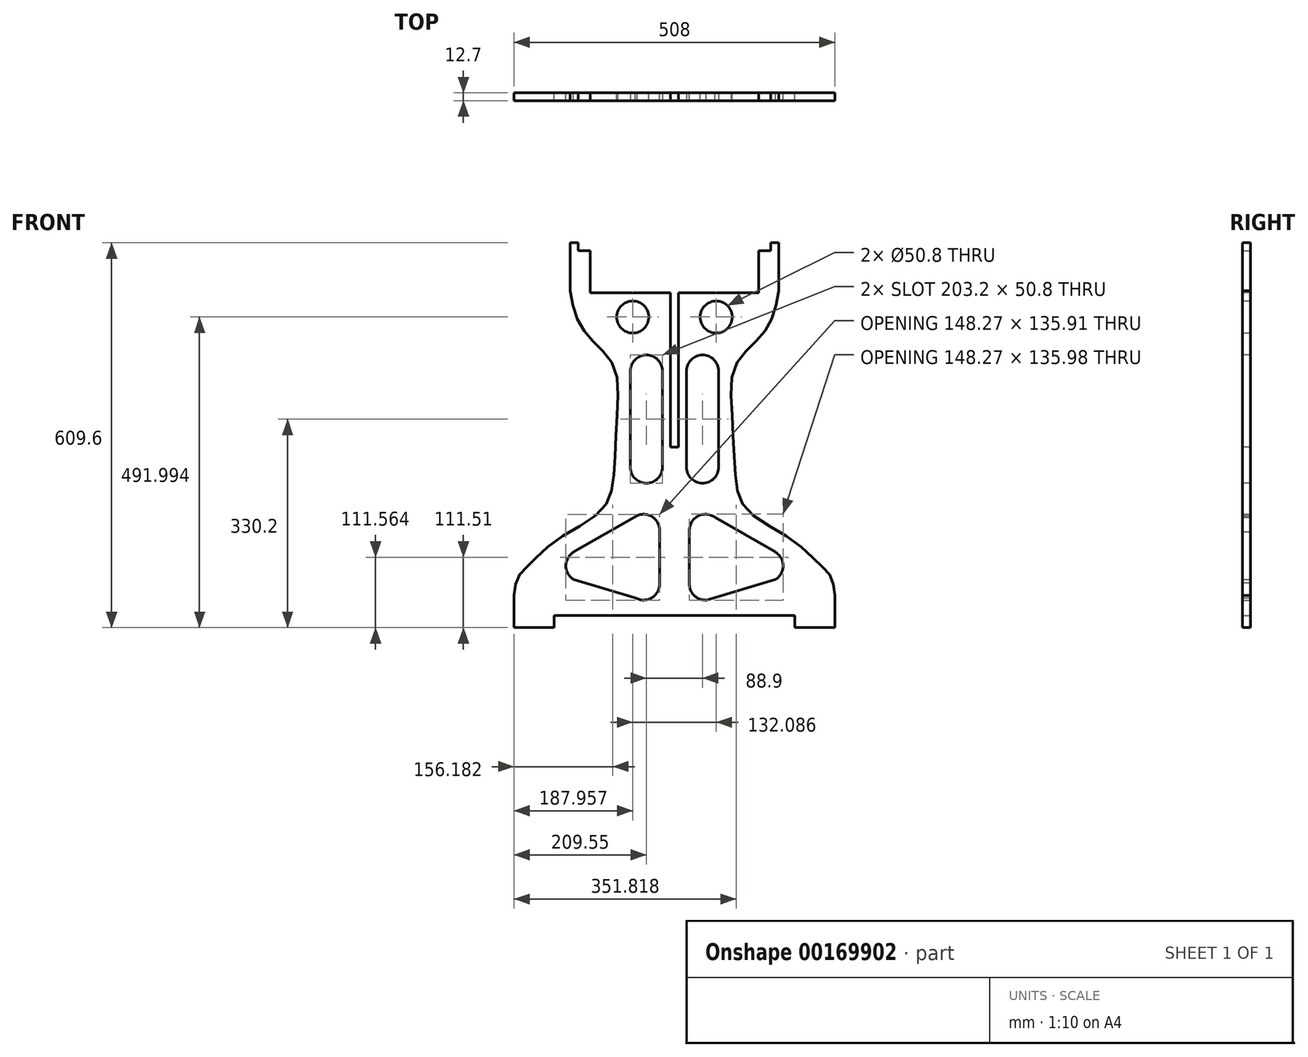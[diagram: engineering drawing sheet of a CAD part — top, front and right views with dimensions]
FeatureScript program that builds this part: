
annotation { "Feature Type Name" : "Feature", "Feature Type Description" : "" }
export const myFeature = defineFeature(function(context is Context, id is Id, definition is map)
    precondition{}
    {
        {
            var Q0;
            Q0=qCreatedBy(makeId("Front.planeOp"),FACE);
            var sketch = newSketch(context, id + "F0", { "sketchPlane" : qUnion([Q0])});
            skLineSegment(sketch, "E0", {"start": v(0, 304.8) * mm, "end": v(0, 530.22) * mm});
            skLineSegment(sketch, "E1", {"start": v(152.4, 609.6) * mm, "end": v(165.1, 609.6) * mm});
            skLineSegment(sketch, "E2", {"start": v(165.1, 609.6) * mm, "end": v(165.1, 533.4) * mm});
            skLineSegment(sketch, "E3", {"start": v(165.1, 609.6) * mm, "end": v(152.4, 609.6) * mm});
            skLineSegment(sketch, "E4", {"start": v(152.4, 609.6) * mm, "end": v(152.4, 596.9) * mm});
            skLineSegment(sketch, "E5", {"start": v(152.4, 596.9) * mm, "end": v(133.35, 596.9) * mm});
            skLineSegment(sketch, "E6", {"start": v(133.35, 596.9) * mm, "end": v(133.35, 530.22) * mm});
            skLineSegment(sketch, "E7", {"start": v(133.35, 530.22) * mm, "end": v(0, 530.22) * mm});
            skLineSegment(sketch, "E8", {"start": v(190.5, 0) * mm, "end": v(254, 0) * mm});
            skLineSegment(sketch, "E9", {"start": v(254, 0) * mm, "end": v(254, 50.8) * mm});
            skLineSegment(sketch, "E10", {"start": v(254, 0) * mm, "end": v(190.5, 0) * mm});
            skLineSegment(sketch, "E11", {"start": v(190.5, 0) * mm, "end": v(190.5, 19.05) * mm});
            skLineSegment(sketch, "E12", {"start": v(190.5, 19.05) * mm, "end": v(6.35, 19.05) * mm});
            skFitSpline(sketch, "E13", {"points": [v(165.1, 533.4) * mm, v(151.94, 484.3) * mm, v(125.02, 449.69) * mm, v(94.25, 409.94) * mm, v(91.68, 327.89) * mm, v(96.81, 235.58) * mm, v(114.76, 186.86) * mm, v(185.28, 139.42) * mm, v(230.15, 99.68) * mm, v(248.1, 79.17) * mm, v(254, 50.8) * mm], "startDerivative": vector(-97.85, -543.75) * mm, "endDerivative": vector(41.55, -423.71) * mm});
            skCircle(sketch, "E14", {"center": v(66.04, 492) * mm, "radius": 25.4 * mm});
            skArc(sketch, "E15", {"start": v(63.82, 174.8) * mm, "mid": v(36.4, 176.26) * mm, "end": v(23.68, 151.93) * mm});
            skArc(sketch, "E16", {"start": v(23.68, 71.21) * mm, "mid": v(30.6, 51.43) * mm, "end": v(50.03, 43.58) * mm});
            skArc(sketch, "E17", {"start": v(160.25, 76.44) * mm, "mid": v(171.96, 98.43) * mm, "end": v(159.24, 119.85) * mm});
            skLineSegment(sketch, "E18", {"start": v(59.37, 177.37) * mm, "end": v(159.24, 119.85) * mm});
            skLineSegment(sketch, "E19", {"start": v(160.25, 76.44) * mm, "end": v(50.03, 43.58) * mm});
            skLineSegment(sketch, "E20", {"start": v(23.68, 156.44) * mm, "end": v(23.68, 66.7) * mm});
            skCircle(sketch, "E21.MirrorC", {"center": v(-66.04, 492) * mm, "radius": 25.4 * mm});
            skLineSegment(sketch, "E22.MirrorCS", {"start": v(-133.35, 530.22) * mm, "end": v(0, 530.22) * mm});
            skLineSegment(sketch, "E23.MirrorCS", {"start": v(-133.35, 596.9) * mm, "end": v(-133.35, 530.22) * mm});
            skLineSegment(sketch, "E24.MirrorCS", {"start": v(-152.4, 596.9) * mm, "end": v(-133.35, 596.9) * mm});
            skLineSegment(sketch, "E25.MirrorCS", {"start": v(-152.4, 609.6) * mm, "end": v(-152.4, 596.9) * mm});
            skLineSegment(sketch, "E26.MirrorCS", {"start": v(-165.1, 609.6) * mm, "end": v(-152.4, 609.6) * mm});
            skLineSegment(sketch, "E27.MirrorCS", {"start": v(-165.1, 609.6) * mm, "end": v(-165.1, 533.4) * mm});
            skFitSpline(sketch, "E28.MirrorCS", {"points": [v(-165.1, 533.4) * mm, v(-151.94, 484.3) * mm, v(-125.02, 449.69) * mm, v(-94.25, 409.94) * mm, v(-91.68, 327.89) * mm, v(-96.81, 235.58) * mm, v(-114.76, 186.86) * mm, v(-185.28, 139.42) * mm, v(-230.15, 99.68) * mm, v(-248.1, 79.17) * mm, v(-254, 50.8) * mm], "startDerivative": vector(97.85, -543.75) * mm, "endDerivative": vector(-41.55, -423.71) * mm});
            skLineSegment(sketch, "E29.MirrorCS", {"start": v(-160.25, 76.44) * mm, "end": v(-62, 47.15) * mm});
            skArc(sketch, "E30.MirrorCS", {"start": v(-160.25, 76.44) * mm, "mid": v(-171.96, 98.43) * mm, "end": v(-159.24, 119.85) * mm});
            skLineSegment(sketch, "E31.MirrorCS", {"start": v(-59.37, 177.37) * mm, "end": v(-159.24, 119.85) * mm});
            skArc(sketch, "E32.MirrorCS", {"start": v(-59.37, 177.37) * mm, "mid": v(-34.24, 174.87) * mm, "end": v(-23.68, 151.93) * mm});
            skLineSegment(sketch, "E33.MirrorCS", {"start": v(-23.68, 151.93) * mm, "end": v(-23.68, 71.21) * mm});
            skArc(sketch, "E34.MirrorCS", {"start": v(-23.68, 71.21) * mm, "mid": v(-35.47, 47.45) * mm, "end": v(-62, 47.15) * mm});
            skLineSegment(sketch, "E35.MirrorCS", {"start": v(-190.5, 19.05) * mm, "end": v(-6.35, 19.05) * mm});
            skLineSegment(sketch, "E36.MirrorCS", {"start": v(-190.5, 0) * mm, "end": v(-190.5, 19.05) * mm});
            skLineSegment(sketch, "E37.MirrorCS", {"start": v(-254, 0) * mm, "end": v(-190.5, 0) * mm});
            skLineSegment(sketch, "E38.MirrorCS", {"start": v(-254, 0) * mm, "end": v(-254, 50.8) * mm});
            skLineSegment(sketch, "E39", {"start": v(6.35, 19.05) * mm, "end": v(6.35, 304.8) * mm});
            skLineSegment(sketch, "E40", {"start": v(6.35, 304.8) * mm, "end": v(-6.35, 304.8) * mm});
            skLineSegment(sketch, "E41", {"start": v(-6.35, 304.8) * mm, "end": v(-6.35, 19.05) * mm});
            skPoint(sketch, "E42.orphan", {"position": v(0, 19.05) * mm});
            skPoint(sketch, "E43.orphan", {"position": v(-50.03, 43.58) * mm});
            skPoint(sketch, "E44.orphan", {"position": v(-23.68, 66.7) * mm});
            skPoint(sketch, "E45.orphan", {"position": v(-63.82, 174.8) * mm});
            skPoint(sketch, "E46.orphan", {"position": v(-23.68, 156.44) * mm});
            skPoint(sketch, "E47.orphan", {"position": v(-146.83, 72.44) * mm});
            skPoint(sketch, "E48.orphan", {"position": v(62, 47.15) * mm});
            skPoint(sketch, "E49.orphan", {"position": v(146.83, 72.44) * mm});
            skSolve(sketch);
        }
        {
            var Q0;
            Q0=qSketchRegion(id+"F0",true);
            extrude(context, id + "F1", {"entities" : qUnion([Q0]), "depth" : 12.7 * mm});
        }
        {
            var Q0;
            Q0=makeQuery(id+"F1.opExtrude","CAP_FACE",FACE,{"disambiguationData":[OSD([sQuery(id+"F0.wireOp",EDGE,"E2"),sQuery(id+"F0.wireOp",EDGE,"E3"),sQuery(id+"F0.wireOp",EDGE,"E4"),sQuery(id+"F0.wireOp",EDGE,"E5"),sQuery(id+"F0.wireOp",EDGE,"E6"),sQuery(id+"F0.wireOp",EDGE,"E7"),sQuery(id+"F0.wireOp",EDGE,"E9"),sQuery(id+"F0.wireOp",EDGE,"E10"),sQuery(id+"F0.wireOp",EDGE,"E11"),sQuery(id+"F0.wireOp",EDGE,"E12"),sQuery(id+"F0.wireOp",EDGE,"E13"),sQuery(id+"F0.wireOp",EDGE,"E14"),sQuery(id+"F0.wireOp",EDGE,"E15"),sQuery(id+"F0.wireOp",EDGE,"E16"),sQuery(id+"F0.wireOp",EDGE,"E17"),sQuery(id+"F0.wireOp",EDGE,"E18"),sQuery(id+"F0.wireOp",EDGE,"E19"),sQuery(id+"F0.wireOp",EDGE,"E20"),sQuery(id+"F0.wireOp",EDGE,"E21.MirrorC"),sQuery(id+"F0.wireOp",EDGE,"E22.MirrorCS"),sQuery(id+"F0.wireOp",EDGE,"E23.MirrorCS"),sQuery(id+"F0.wireOp",EDGE,"E24.MirrorCS"),sQuery(id+"F0.wireOp",EDGE,"E25.MirrorCS"),sQuery(id+"F0.wireOp",EDGE,"E26.MirrorCS"),sQuery(id+"F0.wireOp",EDGE,"E27.MirrorCS"),sQuery(id+"F0.wireOp",EDGE,"E28.MirrorCS"),sQuery(id+"F0.wireOp",EDGE,"E29.MirrorCS"),sQuery(id+"F0.wireOp",EDGE,"E30.MirrorCS"),sQuery(id+"F0.wireOp",EDGE,"E31.MirrorCS"),sQuery(id+"F0.wireOp",EDGE,"E32.MirrorCS"),sQuery(id+"F0.wireOp",EDGE,"E33.MirrorCS"),sQuery(id+"F0.wireOp",EDGE,"E34.MirrorCS"),sQuery(id+"F0.wireOp",EDGE,"E35.MirrorCS"),sQuery(id+"F0.wireOp",EDGE,"E36.MirrorCS"),sQuery(id+"F0.wireOp",EDGE,"E37.MirrorCS"),sQuery(id+"F0.wireOp",EDGE,"E38.MirrorCS"),sQuery(id+"F0.wireOp",EDGE,"E39"),sQuery(id+"F0.wireOp",EDGE,"E40"),sQuery(id+"F0.wireOp",EDGE,"E41")])],"isStart":false});
            var sketch = newSketch(context, id + "F2", { "sketchPlane" : qUnion([Q0])});
            skLineSegment(sketch, "E50", {"start": v(-6.35, 304.8) * mm, "end": v(-6.35, 530.22) * mm});
            skLineSegment(sketch, "E51", {"start": v(-6.35, 530.22) * mm, "end": v(6.35, 530.22) * mm});
            skPoint(sketch, "E51.endSnap0", {"position": v(0, 530.22) * mm});
            skLineSegment(sketch, "E52", {"start": v(6.35, 530.22) * mm, "end": v(6.35, 304.8) * mm});
            skLineSegment(sketch, "E53", {"start": v(6.35, 304.8) * mm, "end": v(-6.35, 304.8) * mm});
            skLineSegment(sketch, "E54", {"start": v(-6.35, 19.05) * mm, "end": v(6.35, 19.05) * mm});
            skLineSegment(sketch, "E55", {"start": v(6.35, 19.05) * mm, "end": v(6.35, 304.8) * mm});
            skLineSegment(sketch, "E56", {"start": v(-6.35, 19.05) * mm, "end": v(-6.35, 304.8) * mm});
            skSolve(sketch);
        }
        {
            var Q0;
            Q0=makeQuery(id+"F2.imprint","IMPRINT",FACE,{"disambiguationData":[TD([[makeQuery(id+"F2.imprint","IMPRINT",EDGE,{"derivedFrom":sQuery(id+"F2.wireOp",EDGE,"E53")}),1.0]])]});
            extrude(context, id + "F3", {"entities" : qUnion([Q0]), "operationType" : NewBodyOperationType.ADD, "oppositeDirection" : true, "depth" : 12.7 * mm});
        }
        {
            var Q0;
            Q0=makeQuery(id+"F3.boolean.opBoolean","MERGE",FACE,{"derivedFrom":[makeQuery(id+"F1.opExtrude","CAP_FACE",FACE,{"disambiguationData":[OSD([sQuery(id+"F0.wireOp",EDGE,"E2"),sQuery(id+"F0.wireOp",EDGE,"E3"),sQuery(id+"F0.wireOp",EDGE,"E4"),sQuery(id+"F0.wireOp",EDGE,"E5"),sQuery(id+"F0.wireOp",EDGE,"E6"),sQuery(id+"F0.wireOp",EDGE,"E7"),sQuery(id+"F0.wireOp",EDGE,"E9"),sQuery(id+"F0.wireOp",EDGE,"E10"),sQuery(id+"F0.wireOp",EDGE,"E11"),sQuery(id+"F0.wireOp",EDGE,"E12"),sQuery(id+"F0.wireOp",EDGE,"E13"),sQuery(id+"F0.wireOp",EDGE,"E14"),sQuery(id+"F0.wireOp",EDGE,"E15"),sQuery(id+"F0.wireOp",EDGE,"E16"),sQuery(id+"F0.wireOp",EDGE,"E17"),sQuery(id+"F0.wireOp",EDGE,"E18"),sQuery(id+"F0.wireOp",EDGE,"E19"),sQuery(id+"F0.wireOp",EDGE,"E20"),sQuery(id+"F0.wireOp",EDGE,"E21.MirrorC"),sQuery(id+"F0.wireOp",EDGE,"E22.MirrorCS"),sQuery(id+"F0.wireOp",EDGE,"E23.MirrorCS"),sQuery(id+"F0.wireOp",EDGE,"E24.MirrorCS"),sQuery(id+"F0.wireOp",EDGE,"E25.MirrorCS"),sQuery(id+"F0.wireOp",EDGE,"E26.MirrorCS"),sQuery(id+"F0.wireOp",EDGE,"E27.MirrorCS"),sQuery(id+"F0.wireOp",EDGE,"E28.MirrorCS"),sQuery(id+"F0.wireOp",EDGE,"E29.MirrorCS"),sQuery(id+"F0.wireOp",EDGE,"E30.MirrorCS"),sQuery(id+"F0.wireOp",EDGE,"E31.MirrorCS"),sQuery(id+"F0.wireOp",EDGE,"E32.MirrorCS"),sQuery(id+"F0.wireOp",EDGE,"E33.MirrorCS"),sQuery(id+"F0.wireOp",EDGE,"E34.MirrorCS"),sQuery(id+"F0.wireOp",EDGE,"E35.MirrorCS"),sQuery(id+"F0.wireOp",EDGE,"E36.MirrorCS"),sQuery(id+"F0.wireOp",EDGE,"E37.MirrorCS"),sQuery(id+"F0.wireOp",EDGE,"E38.MirrorCS"),sQuery(id+"F0.wireOp",EDGE,"E39"),sQuery(id+"F0.wireOp",EDGE,"E40"),sQuery(id+"F0.wireOp",EDGE,"E41")])],"isStart":false}),makeQuery(id+"F3.opExtrude","CAP_FACE",FACE,{"disambiguationData":[OSD([sQuery(id+"F2.wireOp",EDGE,"E53"),sQuery(id+"F2.wireOp",EDGE,"E54"),sQuery(id+"F2.wireOp",EDGE,"E55"),sQuery(id+"F2.wireOp",EDGE,"E56")])],"isStart":true})]});
            var sketch = newSketch(context, id + "F4", { "sketchPlane" : qUnion([Q0])});
            skLineSegment(sketch, "E57", {"start": v(0, 609.6) * mm, "end": v(-6.35, 609.6) * mm});
            skLineSegment(sketch, "E58", {"start": v(-6.35, 609.6) * mm, "end": v(-6.35, 285.75) * mm});
            skLineSegment(sketch, "E59", {"start": v(-6.35, 285.75) * mm, "end": v(6.35, 285.75) * mm});
            skLineSegment(sketch, "E60", {"start": v(6.35, 285.75) * mm, "end": v(6.35, 609.6) * mm});
            skLineSegment(sketch, "E61", {"start": v(6.35, 609.6) * mm, "end": v(0, 609.6) * mm});
            skSolve(sketch);
        }
        {
            var Q0;
            Q0 = qSketchRegion(id + "F4", true);
            extrude(context, id + "F5", {"entities" : qUnion([Q0]), "operationType" : NewBodyOperationType.REMOVE, "oppositeDirection" : true, "depth" : 25.4 * mm});
        }
        {
            var Q0;
            Q0=makeQuery(id+"F3.boolean.opBoolean","MERGE",FACE,{"derivedFrom":[makeQuery(id+"F1.opExtrude","CAP_FACE",FACE,{"disambiguationData":[OSD([sQuery(id+"F0.wireOp",EDGE,"E2"),sQuery(id+"F0.wireOp",EDGE,"E3"),sQuery(id+"F0.wireOp",EDGE,"E4"),sQuery(id+"F0.wireOp",EDGE,"E5"),sQuery(id+"F0.wireOp",EDGE,"E6"),sQuery(id+"F0.wireOp",EDGE,"E7"),sQuery(id+"F0.wireOp",EDGE,"E9"),sQuery(id+"F0.wireOp",EDGE,"E10"),sQuery(id+"F0.wireOp",EDGE,"E11"),sQuery(id+"F0.wireOp",EDGE,"E12"),sQuery(id+"F0.wireOp",EDGE,"E13"),sQuery(id+"F0.wireOp",EDGE,"E14"),sQuery(id+"F0.wireOp",EDGE,"E15"),sQuery(id+"F0.wireOp",EDGE,"E16"),sQuery(id+"F0.wireOp",EDGE,"E17"),sQuery(id+"F0.wireOp",EDGE,"E18"),sQuery(id+"F0.wireOp",EDGE,"E19"),sQuery(id+"F0.wireOp",EDGE,"E20"),sQuery(id+"F0.wireOp",EDGE,"E21.MirrorC"),sQuery(id+"F0.wireOp",EDGE,"E22.MirrorCS"),sQuery(id+"F0.wireOp",EDGE,"E23.MirrorCS"),sQuery(id+"F0.wireOp",EDGE,"E24.MirrorCS"),sQuery(id+"F0.wireOp",EDGE,"E25.MirrorCS"),sQuery(id+"F0.wireOp",EDGE,"E26.MirrorCS"),sQuery(id+"F0.wireOp",EDGE,"E27.MirrorCS"),sQuery(id+"F0.wireOp",EDGE,"E28.MirrorCS"),sQuery(id+"F0.wireOp",EDGE,"E29.MirrorCS"),sQuery(id+"F0.wireOp",EDGE,"E30.MirrorCS"),sQuery(id+"F0.wireOp",EDGE,"E31.MirrorCS"),sQuery(id+"F0.wireOp",EDGE,"E32.MirrorCS"),sQuery(id+"F0.wireOp",EDGE,"E33.MirrorCS"),sQuery(id+"F0.wireOp",EDGE,"E34.MirrorCS"),sQuery(id+"F0.wireOp",EDGE,"E35.MirrorCS"),sQuery(id+"F0.wireOp",EDGE,"E36.MirrorCS"),sQuery(id+"F0.wireOp",EDGE,"E37.MirrorCS"),sQuery(id+"F0.wireOp",EDGE,"E38.MirrorCS"),sQuery(id+"F0.wireOp",EDGE,"E39"),sQuery(id+"F0.wireOp",EDGE,"E40"),sQuery(id+"F0.wireOp",EDGE,"E41")])],"isStart":false}),makeQuery(id+"F3.opExtrude","CAP_FACE",FACE,{"disambiguationData":[OSD([sQuery(id+"F2.wireOp",EDGE,"E53"),sQuery(id+"F2.wireOp",EDGE,"E54"),sQuery(id+"F2.wireOp",EDGE,"E55"),sQuery(id+"F2.wireOp",EDGE,"E56")])],"isStart":true})]});
            var sketch = newSketch(context, id + "F6", { "sketchPlane" : qUnion([Q0])});
            skLineSegment(sketch, "E62", {"start": v(0, 0) * mm, "end": v(0, 604.52) * mm});
            skArc(sketch, "E63", {"start": v(-19.05, 406.4) * mm, "mid": v(-44.45, 431.8) * mm, "end": v(-69.85, 406.4) * mm});
            skArc(sketch, "E64", {"start": v(69.85, 406.4) * mm, "mid": v(44.45, 431.8) * mm, "end": v(19.05, 406.4) * mm});
            skArc(sketch, "E65", {"start": v(-69.85, 254) * mm, "mid": v(-44.45, 228.6) * mm, "end": v(-19.05, 254) * mm});
            skArc(sketch, "E66", {"start": v(19.05, 254) * mm, "mid": v(44.45, 228.6) * mm, "end": v(69.85, 254) * mm});
            skLineSegment(sketch, "E67", {"start": v(-69.85, 406.4) * mm, "end": v(-69.85, 254) * mm});
            skLineSegment(sketch, "E68", {"start": v(-19.05, 406.4) * mm, "end": v(-19.05, 254) * mm});
            skLineSegment(sketch, "E69", {"start": v(19.05, 254) * mm, "end": v(19.05, 406.4) * mm});
            skLineSegment(sketch, "E70", {"start": v(69.85, 406.4) * mm, "end": v(69.85, 254) * mm});
            skSolve(sketch);
        }
        {
            var Q0;
            Q0 = qSketchRegion(id + "F6", true);
            extrude(context, id + "F7", {"entities" : qUnion([Q0]), "operationType" : NewBodyOperationType.REMOVE, "oppositeDirection" : true, "depth" : 25.4 * mm});
        }
    });
